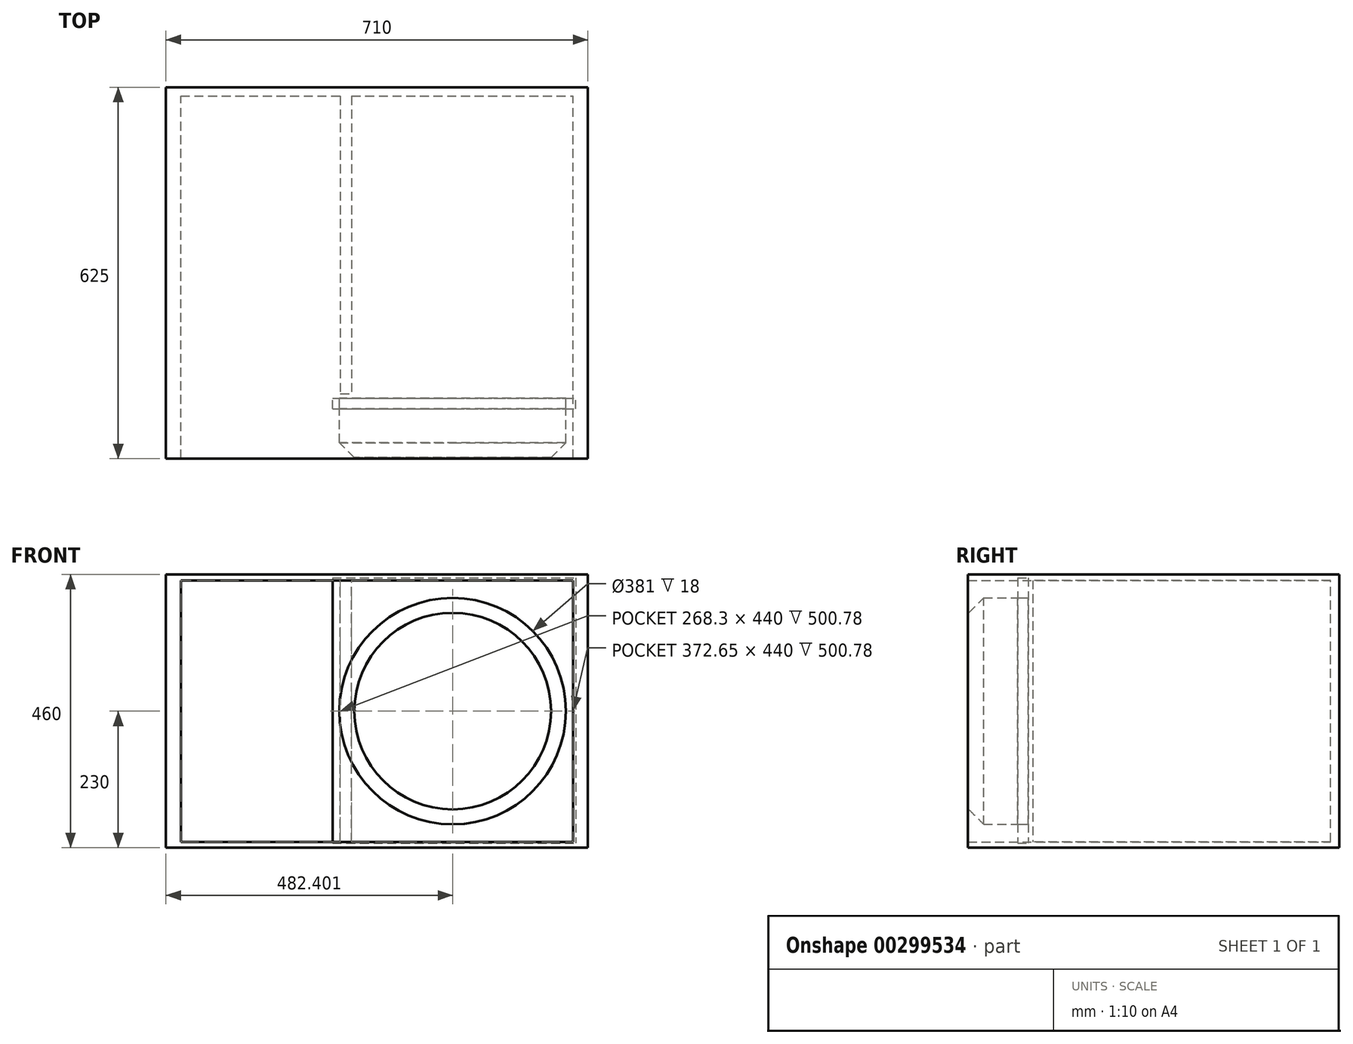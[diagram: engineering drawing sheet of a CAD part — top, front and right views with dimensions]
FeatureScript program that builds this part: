
annotation { "Feature Type Name" : "Feature", "Feature Type Description" : "" }
export const myFeature = defineFeature(function(context is Context, id is Id, definition is map)
    precondition{}
    {
        {
            var Q0;
            Q0=qCreatedBy(makeId("Front.planeOp"),FACE);
            var sketch = newSketch(context, id + "F0", { "sketchPlane" : qUnion([Q0])});
            skLineSegment(sketch, "E0.bottom", {"start": v(-355, 230) * mm, "end": v(355, 230) * mm});
            skLineSegment(sketch, "E0.top", {"start": v(-355, -230) * mm, "end": v(355, -230) * mm});
            skLineSegment(sketch, "E0.left", {"start": v(-355, 230) * mm, "end": v(-355, -230) * mm});
            skLineSegment(sketch, "E0.right", {"start": v(355, 230) * mm, "end": v(355, -230) * mm});
            skPoint(sketch, "E0.middle", {"position": v(0, 0) * mm});
            skLineSegment(sketch, "E1.bottom", {"start": v(-330, 220) * mm, "end": v(330, 220) * mm});
            skLineSegment(sketch, "E1.top", {"start": v(-330, -220) * mm, "end": v(330, -220) * mm});
            skLineSegment(sketch, "E1.left", {"start": v(-330, 220) * mm, "end": v(-330, -220) * mm});
            skLineSegment(sketch, "E1.right", {"start": v(330, 220) * mm, "end": v(330, -220) * mm});
            skLineSegment(sketch, "E2.bottom", {"start": v(-355, 230) * mm, "end": v(-295, 230) * mm});
            skLineSegment(sketch, "E2.top", {"start": v(-355, 245) * mm, "end": v(-295, 245) * mm});
            skLineSegment(sketch, "E2.left", {"start": v(-355, 230) * mm, "end": v(-355, 245) * mm});
            skLineSegment(sketch, "E2.right", {"start": v(-295, 230) * mm, "end": v(-295, 245) * mm});
            skLineSegment(sketch, "E3.bottom", {"start": v(355, 230) * mm, "end": v(295, 230) * mm});
            skLineSegment(sketch, "E3.top", {"start": v(355, 245) * mm, "end": v(295, 245) * mm});
            skLineSegment(sketch, "E3.left", {"start": v(355, 230) * mm, "end": v(355, 245) * mm});
            skLineSegment(sketch, "E3.right", {"start": v(295, 230) * mm, "end": v(295, 245) * mm});
            skLineSegment(sketch, "E4.bottom", {"start": v(355, -230) * mm, "end": v(295, -230) * mm});
            skLineSegment(sketch, "E4.top", {"start": v(355, -245) * mm, "end": v(295, -245) * mm});
            skLineSegment(sketch, "E4.left", {"start": v(355, -230) * mm, "end": v(355, -245) * mm});
            skLineSegment(sketch, "E4.right", {"start": v(295, -230) * mm, "end": v(295, -245) * mm});
            skLineSegment(sketch, "E5.bottom", {"start": v(-355, -230) * mm, "end": v(-295, -230) * mm});
            skLineSegment(sketch, "E5.top", {"start": v(-355, -245) * mm, "end": v(-295, -245) * mm});
            skLineSegment(sketch, "E5.left", {"start": v(-355, -230) * mm, "end": v(-355, -245) * mm});
            skLineSegment(sketch, "E5.right", {"start": v(-295, -230) * mm, "end": v(-295, -245) * mm});
            skSolve(sketch);
        }
        {
            var Q0;
            Q0=makeQuery(id+"F0.imprint","IMPRINT",FACE,{"disambiguationData":[TD([[makeQuery(id+"F0.imprint","IMPRINT",EDGE,{"derivedFrom":sQuery(id+"F0.wireOp",EDGE,"E2.bottom")}),1.0]])]});
            var Q1;
            Q1=makeQuery(id+"F0.imprint","IMPRINT",FACE,{"disambiguationData":[TD([[makeQuery(id+"F0.imprint","IMPRINT",EDGE,{"derivedFrom":sQuery(id+"F0.wireOp",EDGE,"E3.bottom")}),-1.0]])]});
            var Q2;
            Q2=makeQuery(id+"F0.imprint","IMPRINT",FACE,{"disambiguationData":[TD([[makeQuery(id+"F0.imprint","IMPRINT",EDGE,{"derivedFrom":sQuery(id+"F0.wireOp",EDGE,"E4.bottom")}),1.0]])]});
            var Q3;
            Q3=makeQuery(id+"F0.imprint","IMPRINT",FACE,{"disambiguationData":[TD([[makeQuery(id+"F0.imprint","IMPRINT",EDGE,{"derivedFrom":sQuery(id+"F0.wireOp",EDGE,"E5.bottom")}),-1.0]])]});
            var Q4;
            Q4=makeQuery(id+"F0.imprint","IMPRINT",FACE,{"disambiguationData":[TD([[makeQuery(id+"F0.imprint","IMPRINT",EDGE,{"derivedFrom":sQuery(id+"F0.wireOp",EDGE,"E0.bottom")}),-1.0]])]});
            extrude(context, id + "F1", {"entities" : qUnion([Q0, Q1, Q2, Q3, Q4]), "depth" : 625 * mm});
        }
        {
            var Q0;
            Q0=makeQuery(id+"F0.imprint","IMPRINT",FACE,{"disambiguationData":[TD([[makeQuery(id+"F0.imprint","IMPRINT",EDGE,{"derivedFrom":sQuery(id+"F0.wireOp",EDGE,"E0.bottom")}),-1.0]])]});
            var Q1;
            Q1=makeQuery(id+"F0.imprint","IMPRINT",FACE,{"disambiguationData":[TD([[makeQuery(id+"F0.imprint","IMPRINT",EDGE,{"derivedFrom":sQuery(id+"F0.wireOp",EDGE,"E1.bottom")}),-1.0]])]});
            extrude(context, id + "F2", {"entities" : qUnion([Q0, Q1]), "operationType" : NewBodyOperationType.ADD, "depth" : 15 * mm});
        }
        {
            var Q0;
            Q0=makeQuery(id+"F1.opExtrude","CAP_FACE",FACE,{"disambiguationData":[OSD([sQuery(id+"F0.wireOp",EDGE,"E0.bottom"),sQuery(id+"F0.wireOp",EDGE,"E0.top"),sQuery(id+"F0.wireOp",EDGE,"E0.left"),sQuery(id+"F0.wireOp",EDGE,"E0.right"),sQuery(id+"F0.wireOp",EDGE,"E1.bottom"),sQuery(id+"F0.wireOp",EDGE,"E1.top"),sQuery(id+"F0.wireOp",EDGE,"E1.left"),sQuery(id+"F0.wireOp",EDGE,"E1.right"),sQuery(id+"F0.wireOp",EDGE,"E2.top"),sQuery(id+"F0.wireOp",EDGE,"E2.left"),sQuery(id+"F0.wireOp",EDGE,"E2.right"),sQuery(id+"F0.wireOp",EDGE,"E3.top"),sQuery(id+"F0.wireOp",EDGE,"E3.left"),sQuery(id+"F0.wireOp",EDGE,"E3.right"),sQuery(id+"F0.wireOp",EDGE,"E4.top"),sQuery(id+"F0.wireOp",EDGE,"E4.left"),sQuery(id+"F0.wireOp",EDGE,"E4.right"),sQuery(id+"F0.wireOp",EDGE,"E5.top"),sQuery(id+"F0.wireOp",EDGE,"E5.left"),sQuery(id+"F0.wireOp",EDGE,"E5.right")])],"isStart":false});
            cPlane(context, id + "F3", {"entities" : qUnion([Q0]), "cplaneType" : CPlaneType.OFFSET, "offset" : 101.6 * mm, "oppositeDirection" : true, "width" : 150 * mm, "height" : 150 * mm});
        }
        {
            var Q0;
            Q0=qCreatedBy(id+"F3.planeOp",FACE);
            var sketch = newSketch(context, id + "F4", { "sketchPlane" : qUnion([Q0])});
            skCircle(sketch, "E6", {"center": v(127.4, 0) * mm, "radius": 190.5 * mm});
            skLineSegment(sketch, "E7.bottom", {"start": v(-74.57, 224.47) * mm, "end": v(334.43, 224.47) * mm});
            skLineSegment(sketch, "E7.top", {"start": v(-74.57, -222.26) * mm, "end": v(334.43, -222.26) * mm});
            skLineSegment(sketch, "E7.left", {"start": v(-74.57, 224.47) * mm, "end": v(-74.57, -222.26) * mm});
            skLineSegment(sketch, "E7.right", {"start": v(334.43, 224.47) * mm, "end": v(334.43, -222.26) * mm});
            skSolve(sketch);
        }
        {
            var Q0;
            Q0=makeQuery(id+"F4.imprint","IMPRINT",FACE,{"disambiguationData":[TD([[makeQuery(id+"F4.imprint","IMPRINT",EDGE,{"derivedFrom":sQuery(id+"F4.wireOp",EDGE,"E6")}),1.0]])]});
            extrude(context, id + "F5", {"entities" : qUnion([Q0]), "depth" : 100 * mm});
        }
        {
            var Q0;
            Q0=makeQuery(id+"F5.opExtrude","CAP_EDGE",EDGE,{"disambiguationData":[OSD([sQuery(id+"F4.wireOp",EDGE,"E6")])],"isStart":false});
            chamfer(context, id + "F6", {"entities" : qUnion([Q0]), "width" : 25 * mm, "tangentPropagation" : true});
        }
        {
            var Q0;
            Q0 = qSketchRegion(id + "F4", true);
            extrude(context, id + "F7", {"entities" : qUnion([Q0]), "depth" : 18 * mm});
        }
        {
            var Q0;
            Q0=makeQuery(id+"F1.opExtrude","SWEPT_FACE",FACE,{"disambiguationData":[OSD([sQuery(id+"F0.wireOp",EDGE,"E1.top")])]});
            var sketch = newSketch(context, id + "F8", { "sketchPlane" : qUnion([Q0])});
            skLineSegment(sketch, "E8.bottom", {"start": v(-61.7, 0) * mm, "end": v(-42.65, 0) * mm});
            skLineSegment(sketch, "E8.top", {"start": v(-61.7, -515.78) * mm, "end": v(-42.65, -515.78) * mm});
            skLineSegment(sketch, "E8.left", {"start": v(-61.7, 0) * mm, "end": v(-61.7, -515.78) * mm});
            skLineSegment(sketch, "E8.right", {"start": v(-42.65, 0) * mm, "end": v(-42.65, -515.78) * mm});
            skSolve(sketch);
        }
        {
            var Q0;
            Q0 = qSketchRegion(id + "F8", true);
            extrude(context, id + "F9", {"entities" : qUnion([Q0]), "operationType" : NewBodyOperationType.ADD, "depth" : 440 * mm});
        }
    });
